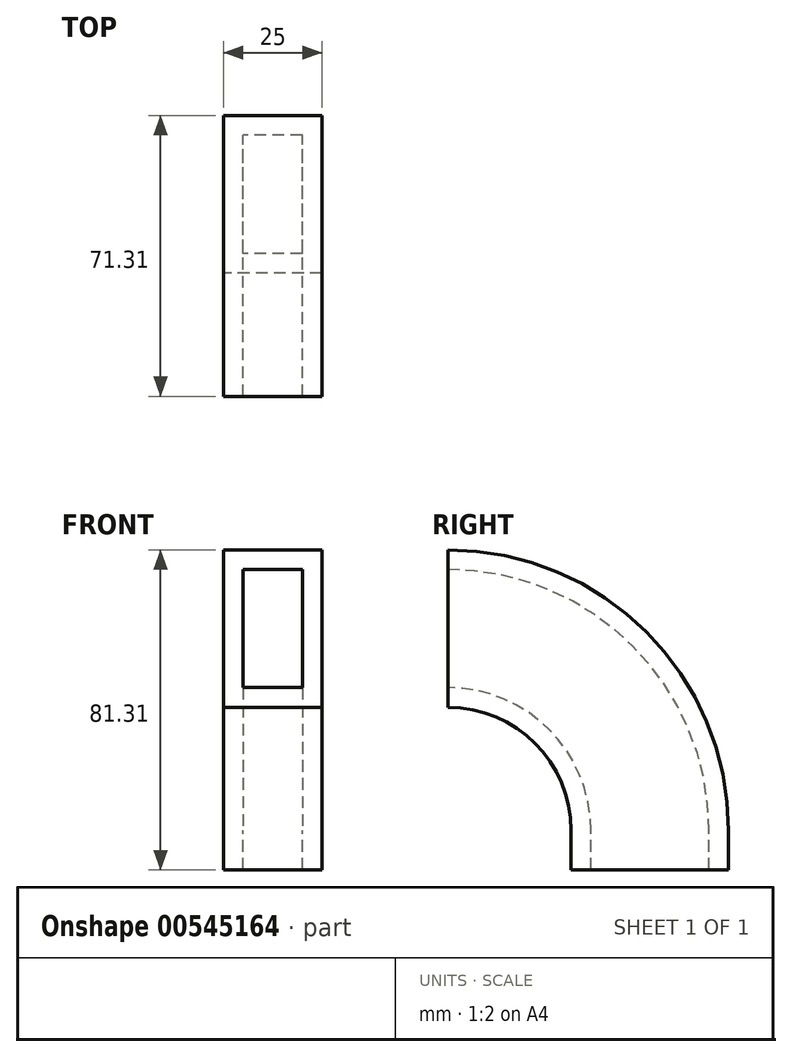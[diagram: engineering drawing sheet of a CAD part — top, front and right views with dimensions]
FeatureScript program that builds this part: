
annotation { "Feature Type Name" : "Feature", "Feature Type Description" : "" }
export const myFeature = defineFeature(function(context is Context, id is Id, definition is map)
    precondition{}
    {
        {
            var Q0;
            Q0=qCreatedBy(makeId("Top.planeOp"),FACE);
            var sketch = newSketch(context, id + "F0", { "sketchPlane" : qUnion([Q0])});
            skLineSegment(sketch, "E0.bottom", {"start": v(12.5, -20) * mm, "end": v(-12.5, -20) * mm});
            skLineSegment(sketch, "E0.top", {"start": v(12.5, 20) * mm, "end": v(-12.5, 20) * mm});
            skLineSegment(sketch, "E0.left", {"start": v(12.5, -20) * mm, "end": v(12.5, 20) * mm});
            skLineSegment(sketch, "E0.right", {"start": v(-12.5, -20) * mm, "end": v(-12.5, 20) * mm});
            skPoint(sketch, "E0.middle", {"position": v(0, 0) * mm});
            skLineSegment(sketch, "E1", {"start": v(-76.4, -51.3) * mm, "end": v(74.21, -51.3) * mm});
            skSolve(sketch);
        }
        {
            var Q0;
            Q0=qCreatedBy(makeId("Top.planeOp"),FACE);
            var sketch = newSketch(context, id + "F1", { "sketchPlane" : qUnion([Q0])});
            skLineSegment(sketch, "E2.bottom", {"start": v(7.5, -15) * mm, "end": v(-7.5, -15) * mm});
            skLineSegment(sketch, "E2.top", {"start": v(7.5, 15) * mm, "end": v(-7.5, 15) * mm});
            skLineSegment(sketch, "E2.left", {"start": v(7.5, -15) * mm, "end": v(7.5, 15) * mm});
            skLineSegment(sketch, "E2.right", {"start": v(-7.5, -15) * mm, "end": v(-7.5, 15) * mm});
            skPoint(sketch, "E2.middle", {"position": v(0, 0) * mm});
            skSolve(sketch);
        }
        {
            var Q0;
            Q0=makeQuery(id+"F0.imprint","IMPRINT",FACE,{"disambiguationData":[TD([[makeQuery(id+"F0.imprint","IMPRINT",EDGE,{"derivedFrom":sQuery(id+"F0.wireOp",EDGE,"E0.bottom")}),-1.0]])]});
            var Q1;
            Q1=sQuery(id+"F0.wireOp",EDGE,"E1");
            revolve(context, id + "F2", {"entities" : qUnion([Q0]), "axis" : qUnion([Q1]), "revolveType" : RevolveType.ONE_DIRECTION, "angle" : 90 * degree});
        }
        {
            var Q0;
            Q0=makeQuery(id+"F1.imprint","IMPRINT",FACE,{"disambiguationData":[TD([[makeQuery(id+"F1.imprint","IMPRINT",EDGE,{"derivedFrom":sQuery(id+"F1.wireOp",EDGE,"E2.bottom")}),-1.0]])]});
            var Q1;
            Q1=sQuery(id+"F0.wireOp",EDGE,"E1");
            revolve(context, id + "F3", {"operationType" : NewBodyOperationType.REMOVE, "entities" : qUnion([Q0]), "axis" : qUnion([Q1]), "revolveType" : RevolveType.ONE_DIRECTION, "angle" : 90 * degree});
        }
        {
            var Q0;
            Q0=makeQuery(id+"F0.imprint","IMPRINT",FACE,{"disambiguationData":[TD([[makeQuery(id+"F0.imprint","IMPRINT",EDGE,{"derivedFrom":sQuery(id+"F0.wireOp",EDGE,"E0.bottom")}),-1.0]])]});
            extrude(context, id + "F4", {"entities" : qUnion([Q0]), "operationType" : NewBodyOperationType.ADD, "oppositeDirection" : true, "depth" : 10 * mm, "offsetDistance" : 25 * mm});
        }
        {
            var Q0;
            Q0 = qSketchRegion(id + "F1", true);
            extrude(context, id + "F5", {"entities" : qUnion([Q0]), "operationType" : NewBodyOperationType.REMOVE, "oppositeDirection" : true, "depth" : 10 * mm, "offsetDistance" : 25 * mm});
        }
    });
